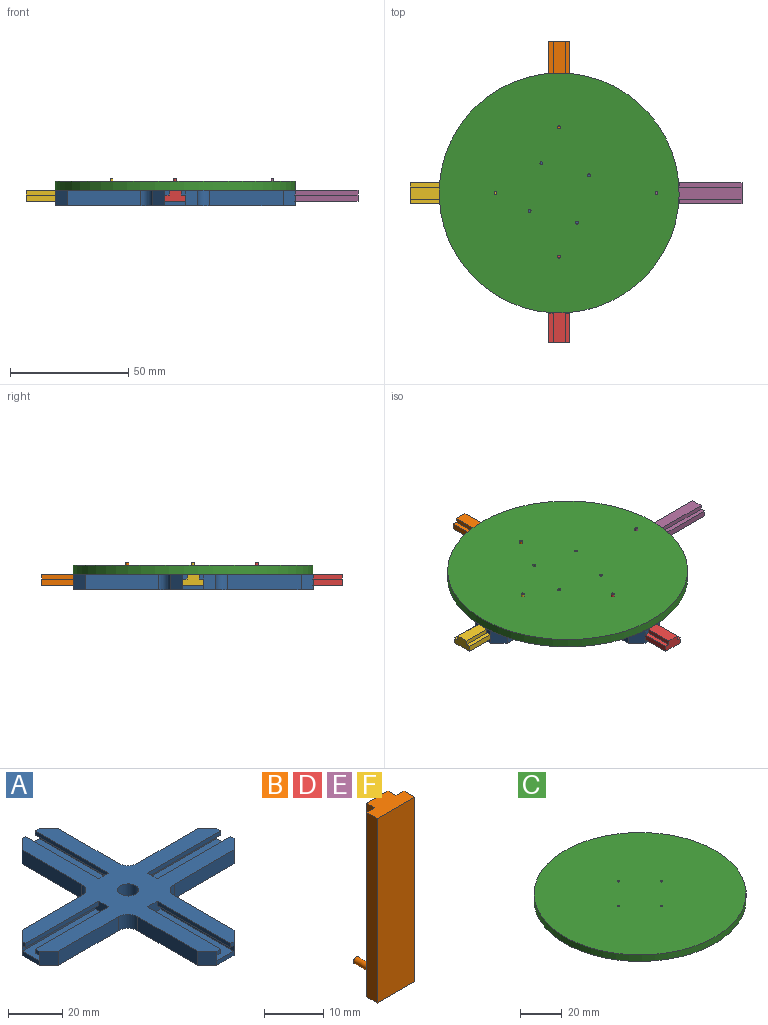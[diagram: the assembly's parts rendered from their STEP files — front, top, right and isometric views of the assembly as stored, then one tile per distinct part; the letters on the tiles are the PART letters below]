
ASSEMBLY  parts=6 mates=5
PART A: 67 faces, bbox 101.6x101.6x6.4 mm
  f0: plane 1.91x1.91mm, normal (0,1,0), area 3.6mm2, adj f8,f47,f48,f61
  f1: plane 8.89x1.91mm, normal (0,1,0), area 16.9mm2, adj f22,f50,f61,f62
  f2: plane 1.91x1.91mm, normal (1,0,0), area 3.6mm2, adj f8,f33,f34,f59
  f3: plane 8.89x1.91mm, normal (1,0,0), area 16.9mm2, adj f22,f36,f59,f60
  f4: plane 8.89x1.91mm, normal (-1,0,0), area 16.9mm2, adj f22,f23,f56,f57
  f5: plane 1.91x1.91mm, normal (-1,0,0), area 3.6mm2, adj f8,f27,f28,f57
  f6: plane 1.91x1.91mm, normal (0,-1,0), area 3.6mm2, adj f8,f41,f42,f55
  f7: plane 8.89x1.91mm, normal (0,-1,0), area 16.9mm2, adj f22,f44,f55,f58
  f8: plane 101.6x101.6mm, normal (0,0,1), area 2605.7mm2, adj f0,f2,f5,f6,f9,f10,f11,f12
  f9: plane 1.91x1.91mm, normal (0,1,0), area 3.6mm2, adj f8,f52,f53,f62
  f10: plane 1.91x1.91mm, normal (-1,0,0), area 3.6mm2, adj f8,f25,f26,f56
  f11: plane 31.12x6.35mm, normal (1,0,0), area 197.6mm2, adj f8,f22,f61,f64
  f12: plane 31.12x6.35mm, normal (-1,0,0), area 197.6mm2, adj f8,f22,f62,f63
  f13: plane 31.12x6.35mm, normal (0,1,0), area 197.6mm2, adj f8,f22,f57,f63
  f14: plane 31.12x6.35mm, normal (0,-1,0), area 197.6mm2, adj f8,f22,f56,f66
  f15: plane 31.12x6.35mm, normal (-1,0,0), area 197.6mm2, adj f8,f22,f55,f66
  f16: plane 1.91x1.91mm, normal (0,-1,0), area 3.6mm2, adj f8,f39,f40,f58
  f17: plane 31.12x6.35mm, normal (1,0,0), area 197.6mm2, adj f8,f22,f58,f65
  f18: plane 31.12x6.35mm, normal (0,-1,0), area 197.6mm2, adj f8,f22,f59,f65
  f19: plane 1.91x1.91mm, normal (1,0,0), area 3.6mm2, adj f8,f31,f32,f60
  f20: plane 31.12x6.35mm, normal (0,1,0), area 197.6mm2, adj f8,f22,f60,f64
  f21: cylinder r=3.87mm len=7.75mm, axis (0,0,-1), area 154.5mm2, adj f8,f22
  f22: plane 101.6x101.6mm, normal (0,0,-1), area 3379.8mm2, adj f1,f3,f4,f7,f11,f12,f13,f14
  f23: plane 38.1x8.89mm, normal (0,0,1), area 338.7mm2, adj f4,f24,f29,f30
  f24: plane 38.1x2.54mm, normal (0,1,0), area 96.8mm2, adj f23,f25,f30,f56
  f25: plane 38.1x1.91mm, normal (0,0,-1), area 72.6mm2, adj f10,f24,f26,f30
  f26: plane 38.1x1.91mm, normal (0,1,0), area 72.6mm2, adj f8,f10,f25,f30
  f27: plane 38.1x1.91mm, normal (0,-1,0), area 72.6mm2, adj f5,f8,f28,f30
  f28: plane 38.1x1.91mm, normal (0,0,-1), area 72.6mm2, adj f5,f27,f29,f30
  f29: plane 38.1x2.54mm, normal (0,-1,0), area 96.8mm2, adj f23,f28,f30,f57
  f30: plane 8.89x4.45mm, normal (-1,0,0), area 32.3mm2, adj f8,f23,f24,f25,f26,f27,f28,f29
  f31: plane 38.1x1.91mm, normal (0,0,-1), area 72.6mm2, adj f19,f32,f37,f38
  f32: plane 38.1x1.91mm, normal (0,-1,0), area 72.6mm2, adj f8,f19,f31,f38
  f33: plane 38.1x1.91mm, normal (0,1,0), area 72.6mm2, adj f2,f8,f34,f38
  f34: plane 38.1x1.91mm, normal (0,0,-1), area 72.6mm2, adj f2,f33,f35,f38
  f35: plane 38.1x2.54mm, normal (0,1,0), area 96.8mm2, adj f34,f36,f38,f59
  f36: plane 38.1x8.89mm, normal (0,0,1), area 338.7mm2, adj f3,f35,f37,f38
  f37: plane 38.1x2.54mm, normal (0,-1,0), area 96.8mm2, adj f31,f36,f38,f60
  f38: plane 8.89x4.45mm, normal (1,0,0), area 32.3mm2, adj f8,f31,f32,f33,f34,f35,f36,f37
  f39: plane 38.1x1.91mm, normal (0,0,-1), area 72.6mm2, adj f16,f40,f45,f46
  f40: plane 38.1x1.91mm, normal (-1,0,0), area 72.6mm2, adj f8,f16,f39,f46
  f41: plane 38.1x1.91mm, normal (1,0,0), area 72.6mm2, adj f6,f8,f42,f46
  f42: plane 38.1x1.91mm, normal (0,0,-1), area 72.6mm2, adj f6,f41,f43,f46
  f43: plane 38.1x2.54mm, normal (1,0,0), area 96.8mm2, adj f42,f44,f46,f55
  f44: plane 38.1x8.89mm, normal (0,0,1), area 338.7mm2, adj f7,f43,f45,f46
  f45: plane 38.1x2.54mm, normal (-1,0,0), area 96.8mm2, adj f39,f44,f46,f58
  f46: plane 8.89x4.45mm, normal (0,-1,0), area 32.3mm2, adj f8,f39,f40,f41,f42,f43,f44,f45
  f47: plane 38.1x1.91mm, normal (-1,0,0), area 72.6mm2, adj f0,f8,f48,f54
  f48: plane 38.1x1.91mm, normal (0,0,-1), area 72.6mm2, adj f0,f47,f49,f54
  f49: plane 38.1x2.54mm, normal (-1,0,0), area 96.8mm2, adj f48,f50,f54,f61
  f50: plane 38.1x8.89mm, normal (0,0,1), area 338.7mm2, adj f1,f49,f51,f54
  f51: plane 38.1x2.54mm, normal (1,0,0), area 96.8mm2, adj f50,f52,f54,f62
  f52: plane 38.1x1.91mm, normal (0,0,-1), area 72.6mm2, adj f9,f51,f53,f54
  f53: plane 38.1x1.91mm, normal (1,0,0), area 72.6mm2, adj f8,f9,f52,f54
  f54: plane 8.89x4.45mm, normal (0,1,0), area 32.3mm2, adj f8,f47,f48,f49,f50,f51,f52,f53
  f55: plane 6.35x5.08mm, normal (-0.71,-0.71,0), area 45.6mm2, adj f6,f7,f8,f15,f22,f43
  f56: plane 6.35x5.08mm, normal (-0.71,-0.71,0), area 45.6mm2, adj f4,f8,f10,f14,f22,f24
  f57: plane 6.35x5.08mm, normal (-0.71,0.71,0), area 45.6mm2, adj f4,f5,f8,f13,f22,f29
  f58: plane 6.35x5.08mm, normal (0.71,-0.71,0), area 45.6mm2, adj f7,f8,f16,f17,f22,f45
  f59: plane 6.35x5.08mm, normal (0.71,-0.71,0), area 45.6mm2, adj f2,f3,f8,f18,f22,f35
  f60: plane 6.35x5.08mm, normal (0.71,0.71,0), area 45.6mm2, adj f3,f8,f19,f20,f22,f37
  f61: plane 6.35x5.08mm, normal (0.71,0.71,0), area 45.6mm2, adj f0,f1,f8,f11,f22,f49
  f62: plane 6.35x5.08mm, normal (-0.71,0.71,0), area 45.6mm2, adj f1,f8,f9,f12,f22,f51
  f63: cylinder r=5.08mm len=6.35mm, axis (0,0,1), area 50.7mm2, adj f8,f12,f13,f22
  f64: cylinder r=5.08mm len=6.35mm, axis (0,0,-1), area 50.7mm2, adj f8,f11,f20,f22
  f65: cylinder r=5.08mm len=6.35mm, axis (0,0,1), area 50.7mm2, adj f8,f17,f18,f22
  f66: cylinder r=5.08mm len=6.35mm, axis (0,0,-1), area 50.7mm2, adj f8,f14,f15,f22
PART B: 12 faces, bbox 8.9x9.5x38.1 mm
  f0: plane 38.1x1.91mm, normal (0,1,0), area 72.6mm2, adj f1,f7,f8,f9
  f1: plane 38.1x1.91mm, normal (1,0,0), area 72.6mm2, adj f0,f2,f8,f9
  f2: plane 38.1x5.08mm, normal (0,1,0), area 192.3mm2, adj f1,f3,f8,f9,f10
  f3: plane 38.1x1.91mm, normal (-1,0,0), area 72.6mm2, adj f2,f4,f8,f9
  f4: plane 38.1x1.91mm, normal (0,1,0), area 72.6mm2, adj f3,f5,f8,f9
  f5: plane 38.1x2.54mm, normal (-1,0,0), area 96.8mm2, adj f4,f6,f8,f9
  f6: plane 38.1x8.89mm, normal (0,-1,0), area 338.7mm2, adj f5,f7,f8,f9
  f7: plane 38.1x2.54mm, normal (1,0,0), area 96.8mm2, adj f0,f6,f8,f9
  f8: plane 8.89x4.45mm, normal (0,0,1), area 32.3mm2, adj f0,f1,f2,f3,f4,f5,f6,f7
  f9: plane 8.89x4.45mm, normal (0,0,-1), area 32.3mm2, adj f0,f1,f2,f3,f4,f5,f6,f7
  f10: cylinder r=0.64mm len=5.08mm, axis (0,-1,0), area 20.3mm2, adj f2,f11
  f11: plane 1.27x1.27mm, normal (0,1,0), area 1.3mm2, adj f10
PART C: 7 faces, bbox 101.6x101.6x3.8 mm
  f0: cylinder r=0.64mm len=3.81mm, axis (0,0,-1), area 15.2mm2, adj f5,f6
  f1: cylinder r=0.64mm len=3.81mm, axis (0,0,-1), area 15.2mm2, adj f5,f6
  f2: cylinder r=0.64mm len=3.81mm, axis (0,0,-1), area 15.2mm2, adj f5,f6
  f3: cylinder r=0.64mm len=3.81mm, axis (0,0,-1), area 15.2mm2, adj f5,f6
  f4: cylinder r=50.8mm len=101.6mm, axis (0,0,-1), area 1216.1mm2, adj f5,f6
  f5: plane 101.6x101.6mm, normal (0,0,1), area 8102.3mm2, adj f0,f1,f2,f3,f4
  f6: plane 101.6x101.6mm, normal (0,0,-1), area 8102.3mm2, adj f0,f1,f2,f3,f4
PART D: same geometry as B
PART E: same geometry as B
PART F: same geometry as B
PLACE A t=(1.24,-37.98,-4.34)mm fixed
PLACE B rot(axis=(0,0.71,0.71),180deg) t=(-3.21,-12.11,-2.43)mm
PLACE C rot(axis=(0.27,-0.96,0),180deg) t=(1.24,-37.98,5.82)mm
PLACE D rot(axis=(1,0,0),90deg) t=(5.68,-62.99,-2.43)mm
PLACE E rot(axis=(0.58,0.58,0.58),120deg) t=(40.54,-33.54,-2.43)mm
PLACE F rot(axis=(0.58,-0.58,-0.58),120deg) t=(-23.8,-42.43,-2.43)mm
MATE slider B.f9 <-> A.f54  axis (0,-1,0) through (1.24,-12.11,-0.49)mm
MATE slider F.f9 <-> A.f30  axis (1,0,0) through (-23.8,-37.98,-0.49)mm
MATE slider E.f9 <-> A.f38  axis (-1,0,0) through (40.54,-37.98,-0.49)mm
MATE revolute A.f21 <-> C.f4  axis (0,0,1) through (1.24,-37.98,2.01)mm
MATE slider D.f9 <-> A.f46  axis (0,1,0) through (1.24,-62.99,-0.49)mm
